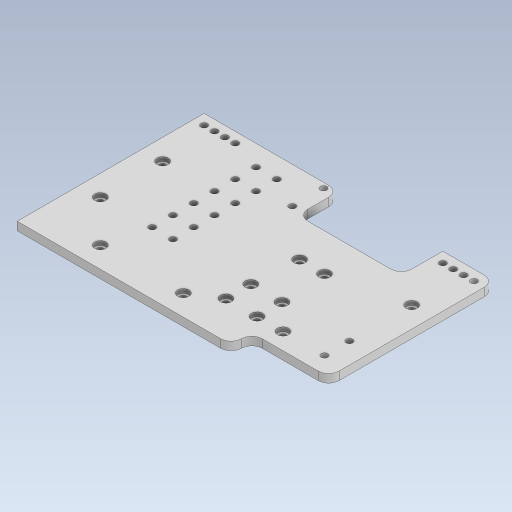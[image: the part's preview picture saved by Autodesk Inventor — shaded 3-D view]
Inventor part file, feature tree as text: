
AUTODESK INVENTOR PART (.ipt)
format: ipt  version: 2023.5 (Build 275446000, 446)  size: 482,816 bytes
history: native  units: mm
features: extrude x2, sketch x1, fillet x1
ambient origin geometry x8: Origin, YZ Plane, XZ Plane, XY Plane, X Axis, Y Axis, Z Axis, Center Point
bodies: Solid1 (feature_tree)
feature tree (4):
  sketch  "Sketch1"  dims[d8=4.0mm d9=0.0mm d10=2.0mm d11=0.0mm d12=140.0mm d13=90.0mm d14=10.0mm d15=10.0mm d16=10.0mm d17=10.0mm d18=10.0mm d19=10.0mm d20=10.0mm d21=3.2mm d22=2.5mm d23=5.0mm d24=3.2mm d25=15.0mm d26=3.2mm d27=3.2mm d28=10.0mm d29=3.2mm d30=10.0mm d31=3.2mm d32=10.0mm d33=10.0mm d35=5.0mm d36=25.0mm d37=3.3mm d38=5.0mm d39=5.0mm d40=3.2mm d41=5.5mm d42=3.2mm d43=3.2mm d44=5.5mm d45=5.5mm d46=10.0mm]
  extrude  "Extrusion1"  Depth=2.0mm TaperAngle=0.0deg
  extrude  "Extrusion2"  Depth=140.0mm
  fillet  "Fillet1"  Radius=90.0mm
